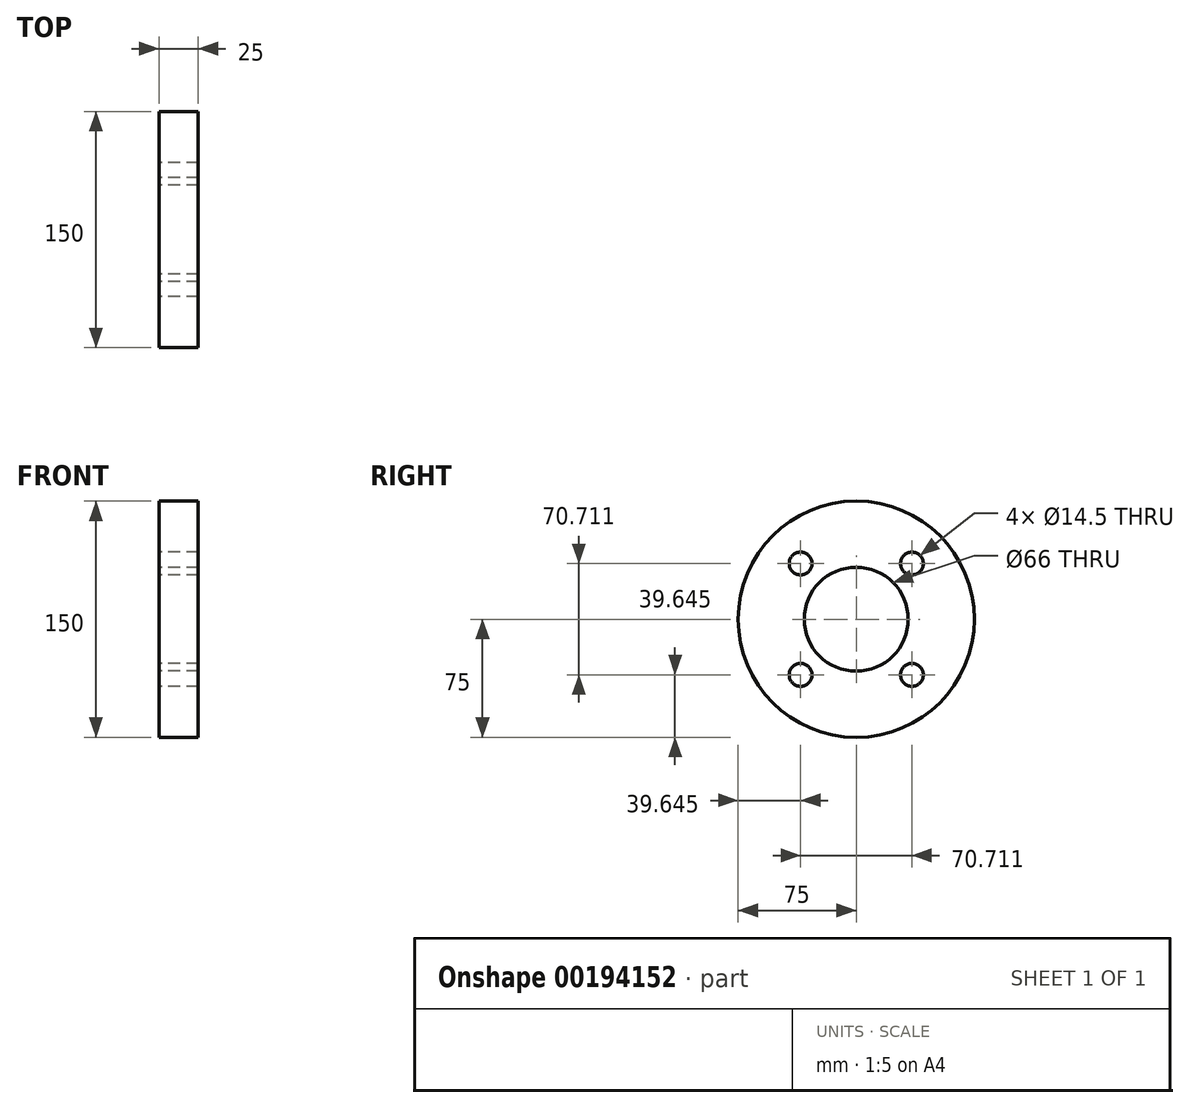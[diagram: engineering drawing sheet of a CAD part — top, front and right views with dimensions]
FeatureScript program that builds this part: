
annotation { "Feature Type Name" : "Feature", "Feature Type Description" : "" }
export const myFeature = defineFeature(function(context is Context, id is Id, definition is map)
    precondition{}
    {
        {
            var Q0;
            Q0=qCreatedBy(makeId("Right.planeOp"),FACE);
            var sketch = newSketch(context, id + "F0", { "sketchPlane" : qUnion([Q0])});
            skCircle(sketch, "E0", {"center": v(0, 0) * mm, "radius": 75 * mm});
            skCircle(sketch, "E1", {"center": v(0, 0) * mm, "radius": 33 * mm});
            skLineSegment(sketch, "E2", {"start": v(0, 0) * mm, "end": v(-62.9, 62.9) * mm, "construction": true});
            skLineSegment(sketch, "E3", {"start": v(0, 0) * mm, "end": v(65.09, 65.09) * mm, "construction": true});
            skLineSegment(sketch, "E4", {"start": v(0, 0) * mm, "end": v(-59.33, -59.33) * mm, "construction": true});
            skLineSegment(sketch, "E5", {"start": v(0, 0) * mm, "end": v(62.29, -62.29) * mm, "construction": true});
            skCircle(sketch, "E6", {"center": v(0, 0) * mm, "radius": 50 * mm, "construction": true});
            skCircle(sketch, "E7", {"center": v(35.36, 35.36) * mm, "radius": 7.25 * mm});
            skCircle(sketch, "E8", {"center": v(35.36, -35.36) * mm, "radius": 7.25 * mm});
            skCircle(sketch, "E9", {"center": v(-35.36, -35.36) * mm, "radius": 7.25 * mm});
            skCircle(sketch, "E10", {"center": v(-35.36, 35.36) * mm, "radius": 7.25 * mm});
            skSolve(sketch);
        }
        {
            var Q0;
            Q0=makeQuery(id+"F0.imprint","IMPRINT",FACE,{"disambiguationData":[TD([[makeQuery(id+"F0.imprint","IMPRINT",EDGE,{"derivedFrom":sQuery(id+"F0.wireOp",EDGE,"E0")}),1.0]])]});
            extrude(context, id + "F1", {"entities" : qUnion([Q0]), "depth" : 25 * mm});
        }
    });
